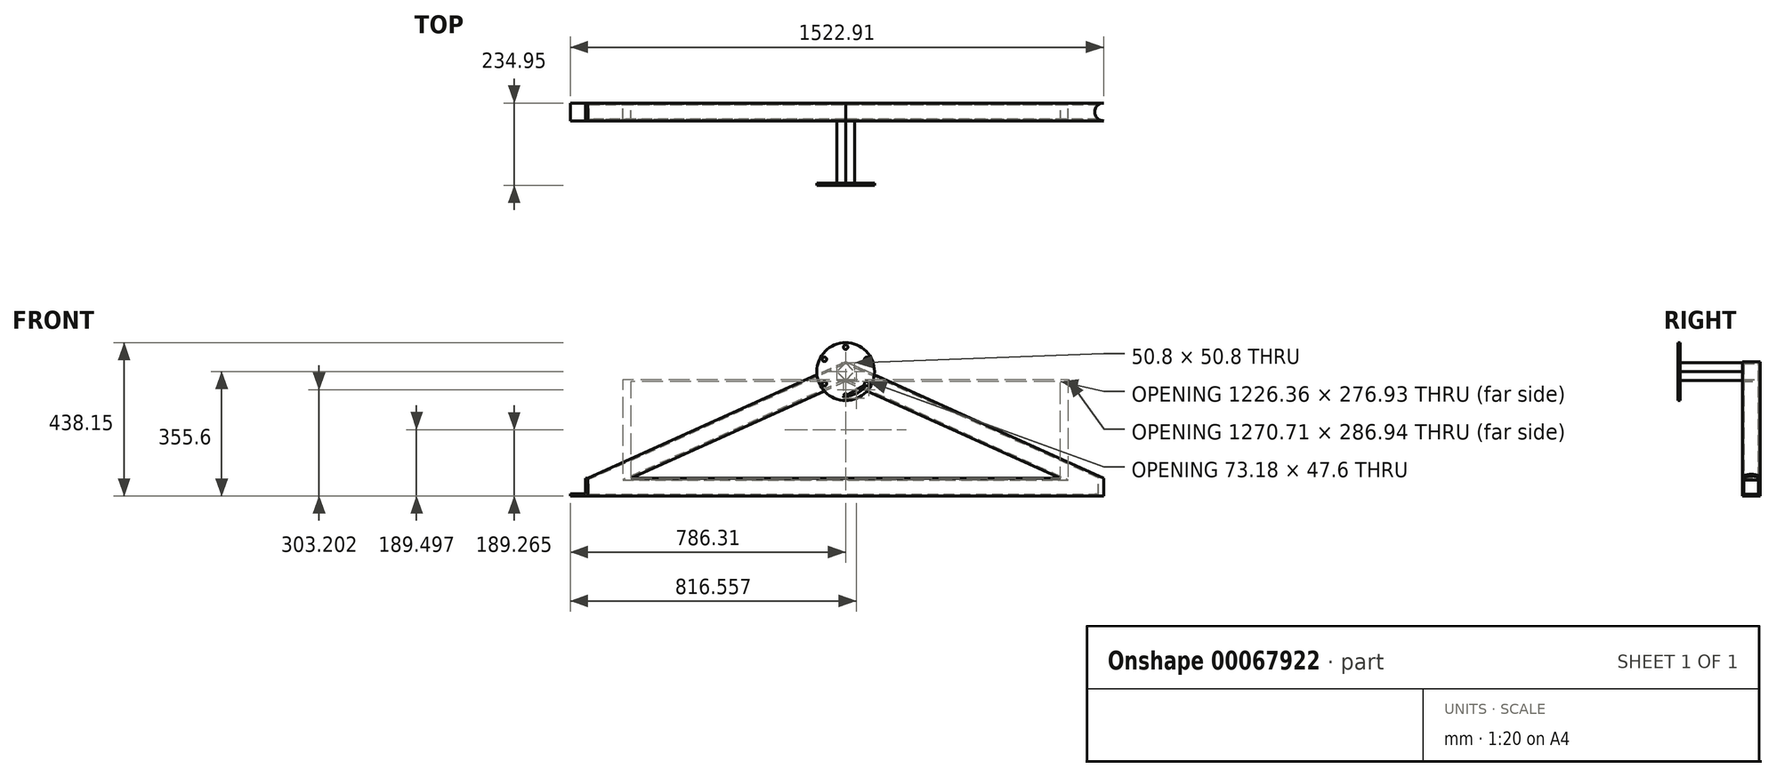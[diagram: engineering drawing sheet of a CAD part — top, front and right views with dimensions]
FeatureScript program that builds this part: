
annotation { "Feature Type Name" : "Feature", "Feature Type Description" : "" }
export const myFeature = defineFeature(function(context is Context, id is Id, definition is map)
    precondition{}
    {
        {
            var Q0;
            Q0=qCreatedBy(makeId("Front.planeOp"),FACE);
            var sketch = newSketch(context, id + "F0", { "sketchPlane" : qUnion([Q0])});
            skLineSegment(sketch, "E0", {"start": v(0, 0) * mm, "end": v(1473.2, 0) * mm});
            skLineSegment(sketch, "E1", {"start": v(1473.2, 0) * mm, "end": v(736.6, 332.67) * mm});
            skLineSegment(sketch, "E2", {"start": v(736.6, 332.67) * mm, "end": v(0, 0) * mm});
            skLineSegment(sketch, "E3", {"start": v(0, -50.8) * mm, "end": v(1473.2, -50.8) * mm});
            skLineSegment(sketch, "E4", {"start": v(1473.2, -50.8) * mm, "end": v(1473.2, 0) * mm});
            skLineSegment(sketch, "E5", {"start": v(0, -50.8) * mm, "end": v(0, 0) * mm});
            skLineSegment(sketch, "E6", {"start": v(736.6, 332.67) * mm, "end": v(736.6, 276.93) * mm});
            skLineSegment(sketch, "E7", {"start": v(736.6, 276.93) * mm, "end": v(1349.78, 0) * mm});
            skLineSegment(sketch, "E8", {"start": v(736.6, 276.93) * mm, "end": v(123.42, 0) * mm});
            skPoint(sketch, "E9", {"position": v(736.6, 304.8) * mm});
            skSolve(sketch);
        }
        {
            var Q0;
            {var subQ0=sQuery(id+"F0.wireOp",EDGE,"E2");Q0=makeQuery(id+"F0.imprint","IMPRINT",FACE,{"disambiguationData":[TD([[makeQuery(id+"F0.imprint","IMPRINT",EDGE,{"derivedFrom":subQ0}),1.0]])]});}
            var Q1;
            {var subQ0=sQuery(id+"F0.wireOp",EDGE,"E1");Q1=makeQuery(id+"F0.imprint","IMPRINT",FACE,{"disambiguationData":[TD([[makeQuery(id+"F0.imprint","IMPRINT",EDGE,{"derivedFrom":subQ0}),1.0]])]});}
            var Q2;
            Q2=makeQuery(id+"F0.imprint","IMPRINT",FACE,{"disambiguationData":[TD([[makeQuery(id+"F0.imprint","IMPRINT",EDGE,{"derivedFrom":sQuery(id+"F0.wireOp",EDGE,"E3")}),1.0]])]});
            extrude(context, id + "F1", {"entities" : qUnion([Q0, Q1, Q2]), "depth" : 50.8 * mm});
        }
        {
            var Q0;
            Q0=makeQuery(id+"F1.opExtrude","SWEPT_FACE",FACE,{"disambiguationData":[OSD([sQuery(id+"F0.wireOp",EDGE,"E4")])]});
            shell(context, id + "F2", {"entities" : qUnion([Q0]), "thickness" : 4.78 * mm});
        }
        {
            var Q0;
            Q0=qCreatedBy(makeId("Top.planeOp"),FACE);
            var sketch = newSketch(context, id + "F3", { "sketchPlane" : qUnion([Q0])});
            skLineSegment(sketch, "E10.0", {"start": v(1473.2, -50.8) * mm, "end": v(1473.2, 0) * mm});
            skPoint(sketch, "E11", {"position": v(1473.2, -25.4) * mm});
            skCircle(sketch, "E12", {"center": v(1473.2, -25.4) * mm, "radius": 25.4 * mm});
            skSolve(sketch);
        }
        {
            var Q0;
            Q0 = qSketchRegion(id + "F3", true);
            extrude(context, id + "F4", {"entities" : qUnion([Q0]), "operationType" : NewBodyOperationType.REMOVE, "endBound" : BoundingType.SYMMETRIC, "oppositeDirection" : true, "depth" : 101.6 * mm});
        }
        {
            var Q0;
            Q0=makeQuery(id+"F1.opExtrude","CAP_FACE",FACE,{"disambiguationData":[OSD([sQuery(id+"F0.wireOp",EDGE,"E0"),sQuery(id+"F0.wireOp",EDGE,"E1"),sQuery(id+"F0.wireOp",EDGE,"E2"),sQuery(id+"F0.wireOp",EDGE,"E3"),sQuery(id+"F0.wireOp",EDGE,"E4"),sQuery(id+"F0.wireOp",EDGE,"E5"),sQuery(id+"F0.wireOp",EDGE,"E7"),sQuery(id+"F0.wireOp",EDGE,"E8")])],"isStart":false});
            var sketch = newSketch(context, id + "F5", { "sketchPlane" : qUnion([Q0])});
            skLineSegment(sketch, "E13.0.0", {"start": v(736.6, 332.67) * mm, "end": v(0, 0) * mm});
            skLineSegment(sketch, "E13.0.1", {"start": v(0, 0) * mm, "end": v(0, -50.8) * mm});
            skLineSegment(sketch, "E13.0.2", {"start": v(0, -50.8) * mm, "end": v(1473.2, -50.8) * mm});
            skLineSegment(sketch, "E13.0.3", {"start": v(1473.2, -50.8) * mm, "end": v(1473.2, 0) * mm});
            skLineSegment(sketch, "E13.0.4", {"start": v(1473.2, 0) * mm, "end": v(736.6, 332.67) * mm});
            skLineSegment(sketch, "E14", {"start": v(736.6, 304.8) * mm, "end": v(762, 304.8) * mm});
            skLineSegment(sketch, "E15", {"start": v(736.6, 304.8) * mm, "end": v(711.2, 304.8) * mm});
            skLineSegment(sketch, "E16", {"start": v(736.6, 304.8) * mm, "end": v(736.6, 330.2) * mm});
            skLineSegment(sketch, "E17", {"start": v(736.6, 304.8) * mm, "end": v(736.6, 279.4) * mm});
            skLineSegment(sketch, "E18", {"start": v(736.6, 279.4) * mm, "end": v(762, 304.8) * mm});
            skLineSegment(sketch, "E19", {"start": v(736.6, 330.2) * mm, "end": v(762, 304.8) * mm});
            skLineSegment(sketch, "E20", {"start": v(736.6, 330.2) * mm, "end": v(711.2, 304.8) * mm});
            skLineSegment(sketch, "E21", {"start": v(736.6, 279.4) * mm, "end": v(711.2, 304.8) * mm});
            skSolve(sketch);
        }
        {
            var Q0;
            Q0=makeQuery(id+"F5.imprint","IMPRINT",FACE,{"disambiguationData":[TD([[makeQuery(id+"F5.imprint","IMPRINT",EDGE,{"derivedFrom":sQuery(id+"F5.wireOp",EDGE,"E15")}),1.0]])]});
            var Q1;
            Q1=makeQuery(id+"F5.imprint","IMPRINT",FACE,{"disambiguationData":[TD([[makeQuery(id+"F5.imprint","IMPRINT",EDGE,{"derivedFrom":sQuery(id+"F5.wireOp",EDGE,"E15")}),-1.0]])]});
            var Q2;
            Q2=makeQuery(id+"F5.imprint","IMPRINT",FACE,{"disambiguationData":[TD([[makeQuery(id+"F5.imprint","IMPRINT",EDGE,{"derivedFrom":sQuery(id+"F5.wireOp",EDGE,"E14")}),1.0]])]});
            var Q3;
            Q3=makeQuery(id+"F5.imprint","IMPRINT",FACE,{"disambiguationData":[TD([[makeQuery(id+"F5.imprint","IMPRINT",EDGE,{"derivedFrom":sQuery(id+"F5.wireOp",EDGE,"E14")}),-1.0]])]});
            extrude(context, id + "F6", {"entities" : qUnion([Q0, Q1, Q2, Q3]), "operationType" : NewBodyOperationType.ADD, "depth" : 177.8 * mm});
        }
        {
            var Q0;
            Q0=makeQuery(id+"F6.opExtrude","CAP_FACE",FACE,{"disambiguationData":[OSD([sQuery(id+"F5.wireOp",EDGE,"E18"),sQuery(id+"F5.wireOp",EDGE,"E19"),sQuery(id+"F5.wireOp",EDGE,"E20"),sQuery(id+"F5.wireOp",EDGE,"E21")])],"isStart":false});
            var sketch = newSketch(context, id + "F7", { "sketchPlane" : qUnion([Q0])});
            skLineSegment(sketch, "E22.0.0", {"start": v(711.2, 304.8) * mm, "end": v(736.6, 279.4) * mm});
            skLineSegment(sketch, "E22.0.1", {"start": v(736.6, 279.4) * mm, "end": v(762, 304.8) * mm});
            skLineSegment(sketch, "E22.0.2", {"start": v(762, 304.8) * mm, "end": v(736.6, 330.2) * mm});
            skLineSegment(sketch, "E22.0.3", {"start": v(736.6, 330.2) * mm, "end": v(711.2, 304.8) * mm});
            skCircle(sketch, "E23", {"center": v(736.6, 304.8) * mm, "radius": 82.55 * mm});
            skCircle(sketch, "E24", {"center": v(736.6, 304.8) * mm, "radius": 69.85 * mm});
            skLineSegment(sketch, "E25", {"start": v(736.6, 304.8) * mm, "end": v(736.6, 374.65) * mm});
            skCircle(sketch, "E26", {"center": v(736.6, 374.65) * mm, "radius": 6.35 * mm});
            skCircle(sketch, "E27.cCircle", {"center": v(736.6, 304.8) * mm, "radius": 69.85 * mm, "construction": true});
            skLineSegment(sketch, "E27.0", {"start": v(736.6, 374.65) * mm, "end": v(797.1, 339.72) * mm});
            skLineSegment(sketch, "E27.1", {"start": v(797.1, 339.72) * mm, "end": v(797.1, 269.88) * mm});
            skLineSegment(sketch, "E27.2", {"start": v(797.1, 269.87) * mm, "end": v(736.6, 234.95) * mm});
            skLineSegment(sketch, "E27.3", {"start": v(736.6, 234.95) * mm, "end": v(676.1, 269.88) * mm});
            skLineSegment(sketch, "E27.4", {"start": v(676.1, 269.88) * mm, "end": v(676.1, 339.73) * mm});
            skLineSegment(sketch, "E27.5", {"start": v(676.1, 339.72) * mm, "end": v(736.6, 374.65) * mm});
            skCircle(sketch, "E28", {"center": v(676.1, 339.73) * mm, "radius": 6.35 * mm});
            skCircle(sketch, "E29", {"center": v(676.1, 269.87) * mm, "radius": 6.35 * mm});
            skCircle(sketch, "E30", {"center": v(736.6, 234.95) * mm, "radius": 6.35 * mm});
            skCircle(sketch, "E31", {"center": v(797.1, 269.88) * mm, "radius": 6.35 * mm});
            skCircle(sketch, "E32", {"center": v(797.1, 339.72) * mm, "radius": 6.35 * mm});
            skSolve(sketch);
        }
        {
            var Q0;
            Q0=makeQuery(id+"F7.imprint","IMPRINT",FACE,{"disambiguationData":[TD([[makeQuery(id+"F7.imprint","IMPRINT",EDGE,{"derivedFrom":sQuery(id+"F7.wireOp",EDGE,"E22.0.0")}),1.0]])]});
            var Q1;
            Q1=makeQuery(id+"F7.imprint","IMPRINT",FACE,{"disambiguationData":[TD([[makeQuery(id+"F7.imprint","IMPRINT",EDGE,{"derivedFrom":sQuery(id+"F7.wireOp",EDGE,"E22.0.0")}),-1.0]])]});
            var Q2;
            Q2=makeQuery(id+"F7.imprint","IMPRINT",FACE,{"disambiguationData":[TD([[makeQuery(id+"F7.imprint","IMPRINT",EDGE,{"derivedFrom":sQuery(id+"F7.wireOp",EDGE,"E23")}),1.0]])]});
            var Q3;
            {var subQ0=sQuery(id+"F7.wireOp",EDGE,"E26");var subQ1=sQuery(id+"F7.wireOp",EDGE,"E24");var subQ2=makeQuery(id+"F7.imprint","INTERSECT",VERTEX,{"disambiguationData":[OD(1.0)],"derivedFrom":[subQ1,subQ0]});Q3=makeQuery(id+"F7.imprint","IMPRINT",FACE,{"disambiguationData":[TD([[makeQuery(id+"F7.imprint","IMPRINT",EDGE,{"disambiguationData":[TD([[subQ2,-1.0]])],"derivedFrom":subQ1}),1.0]])]});}
            var Q4;
            {var subQ0=sQuery(id+"F7.wireOp",EDGE,"E32");var subQ1=sQuery(id+"F7.wireOp",EDGE,"E24");var subQ2=makeQuery(id+"F7.imprint","INTERSECT",VERTEX,{"disambiguationData":[OD(1.0)],"derivedFrom":[subQ1,subQ0]});Q4=makeQuery(id+"F7.imprint","IMPRINT",FACE,{"disambiguationData":[TD([[makeQuery(id+"F7.imprint","IMPRINT",EDGE,{"disambiguationData":[TD([[subQ2,-1.0]])],"derivedFrom":subQ1}),1.0]])]});}
            var Q5;
            {var subQ0=sQuery(id+"F7.wireOp",EDGE,"E32");var subQ1=sQuery(id+"F7.wireOp",EDGE,"E24");var subQ2=makeQuery(id+"F7.imprint","INTERSECT",VERTEX,{"disambiguationData":[OD(0.0)],"derivedFrom":[subQ1,subQ0]});Q5=makeQuery(id+"F7.imprint","IMPRINT",FACE,{"disambiguationData":[TD([[makeQuery(id+"F7.imprint","IMPRINT",EDGE,{"disambiguationData":[TD([[subQ2,1.0]])],"derivedFrom":subQ1}),1.0]])]});}
            var Q6;
            {var subQ0=sQuery(id+"F7.wireOp",EDGE,"E30");var subQ1=sQuery(id+"F7.wireOp",EDGE,"E24");var subQ2=makeQuery(id+"F7.imprint","INTERSECT",VERTEX,{"disambiguationData":[OD(1.0)],"derivedFrom":[subQ1,subQ0]});Q6=makeQuery(id+"F7.imprint","IMPRINT",FACE,{"disambiguationData":[TD([[makeQuery(id+"F7.imprint","IMPRINT",EDGE,{"disambiguationData":[TD([[subQ2,-1.0]])],"derivedFrom":subQ1}),1.0]])]});}
            var Q7;
            {var subQ0=sQuery(id+"F7.wireOp",EDGE,"E29");var subQ1=sQuery(id+"F7.wireOp",EDGE,"E24");var subQ2=makeQuery(id+"F7.imprint","INTERSECT",VERTEX,{"disambiguationData":[OD(1.0)],"derivedFrom":[subQ1,subQ0]});Q7=makeQuery(id+"F7.imprint","IMPRINT",FACE,{"disambiguationData":[TD([[makeQuery(id+"F7.imprint","IMPRINT",EDGE,{"disambiguationData":[TD([[subQ2,-1.0]])],"derivedFrom":subQ1}),1.0]])]});}
            var Q8;
            {var subQ0=sQuery(id+"F7.wireOp",EDGE,"E28");var subQ1=sQuery(id+"F7.wireOp",EDGE,"E24");var subQ2=makeQuery(id+"F7.imprint","INTERSECT",VERTEX,{"disambiguationData":[OD(1.0)],"derivedFrom":[subQ1,subQ0]});Q8=makeQuery(id+"F7.imprint","IMPRINT",FACE,{"disambiguationData":[TD([[makeQuery(id+"F7.imprint","IMPRINT",EDGE,{"disambiguationData":[TD([[subQ2,-1.0]])],"derivedFrom":subQ1}),1.0]])]});}
            extrude(context, id + "F8", {"entities" : qUnion([Q0, Q1, Q2, Q3, Q4, Q5, Q6, Q7, Q8]), "operationType" : NewBodyOperationType.ADD, "depth" : 6.35 * mm});
        }
        {
            var Q0;
            Q0=makeQuery(id+"F1.opExtrude","CAP_FACE",FACE,{"disambiguationData":[OSD([sQuery(id+"F0.wireOp",EDGE,"E0"),sQuery(id+"F0.wireOp",EDGE,"E1"),sQuery(id+"F0.wireOp",EDGE,"E2"),sQuery(id+"F0.wireOp",EDGE,"E3"),sQuery(id+"F0.wireOp",EDGE,"E4"),sQuery(id+"F0.wireOp",EDGE,"E5"),sQuery(id+"F0.wireOp",EDGE,"E7"),sQuery(id+"F0.wireOp",EDGE,"E8")])],"isStart":false});
            var sketch = newSketch(context, id + "F9", { "sketchPlane" : qUnion([Q0])});
            skLineSegment(sketch, "E33.0", {"start": v(0, -50.8) * mm, "end": v(0, 0) * mm});
            skLineSegment(sketch, "E34", {"start": v(0, 0) * mm, "end": v(-6.35, 0) * mm});
            skLineSegment(sketch, "E35", {"start": v(-6.35, 0) * mm, "end": v(-6.35, -44.45) * mm});
            skLineSegment(sketch, "E36", {"start": v(-6.35, -44.45) * mm, "end": v(-49.7, -44.45) * mm});
            skLineSegment(sketch, "E37", {"start": v(-49.7, -44.45) * mm, "end": v(-49.7, -50.8) * mm});
            skLineSegment(sketch, "E38", {"start": v(-49.7, -50.8) * mm, "end": v(0, -50.8) * mm});
            skSolve(sketch);
        }
        {
            var Q0;
            Q0=makeQuery(id+"F9.imprint","IMPRINT",FACE,{"disambiguationData":[TD([[makeQuery(id+"F9.imprint","IMPRINT",EDGE,{"derivedFrom":sQuery(id+"F9.wireOp",EDGE,"E33.0")}),1.0]])]});
            extrude(context, id + "F10", {"entities" : qUnion([Q0]), "oppositeDirection" : true, "depth" : 50.8 * mm});
        }
    });
